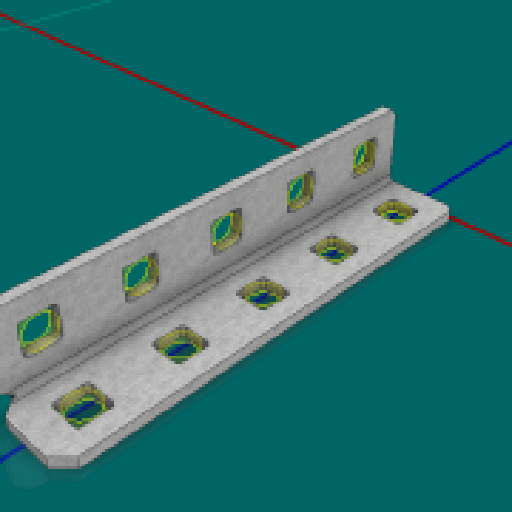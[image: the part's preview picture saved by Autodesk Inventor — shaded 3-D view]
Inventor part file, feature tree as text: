
AUTODESK INVENTOR PART (.ipt)
format: ipt  version: 2025 (Build 290162000, 162)  size: 353,792 bytes
history: native  units: in
note: dims shown in document units (in); Inventor stores cm internally (conversion verified against a paired STEP export)
features: other x29, sketch x2, sheet_metal_op x1
ambient origin geometry x8: Origin, YZ Plane, XZ Plane, XY Plane, X Axis, Y Axis, Z Axis, Center Point
bodies: Solid1 (feature_tree)
feature tree (32):
  other  "Alu Angle 1x1x5.ipt"
  other  "Solid1::Alu Angle 1x1x5.ipt"
  other  "TaggingFeature1"
  sketch  "Sketch1"  dims[d0=0.3937in]
  sketch  "Sketch2"  dims[d1=0.0625in]
  sheet_metal_op  "Body Pattern Sketch"
  other  "Arc Length"
  other  "Diagonal Plane"
  other  "Srf1"
  other  "Srf2"
  other  "Srf3"
  other  "Srf4"
  other  "Srf5"
  other  "Srf6"
  other  "Srf7"
  other  "Srf8"
  other  "Srf9"
  other  "Srf10"
  other  "Srf11"
  other  "Srf12"
  other  "Srf91::Derived"
  other  "Srf92::Derived"
  other  "Srf856::Derived"
  other  "Srf857::Derived"
  other  "Srf858::Derived"
  other  "Srf859::Derived"
  other  "Srf1275::Derived"
  other  "Srf1276::Derived"
  other  "Srf1278::Derived"
  other  "Srf1279::Derived"
  other  "Srf1280::Derived"
  other  "Srf1281::Derived"
